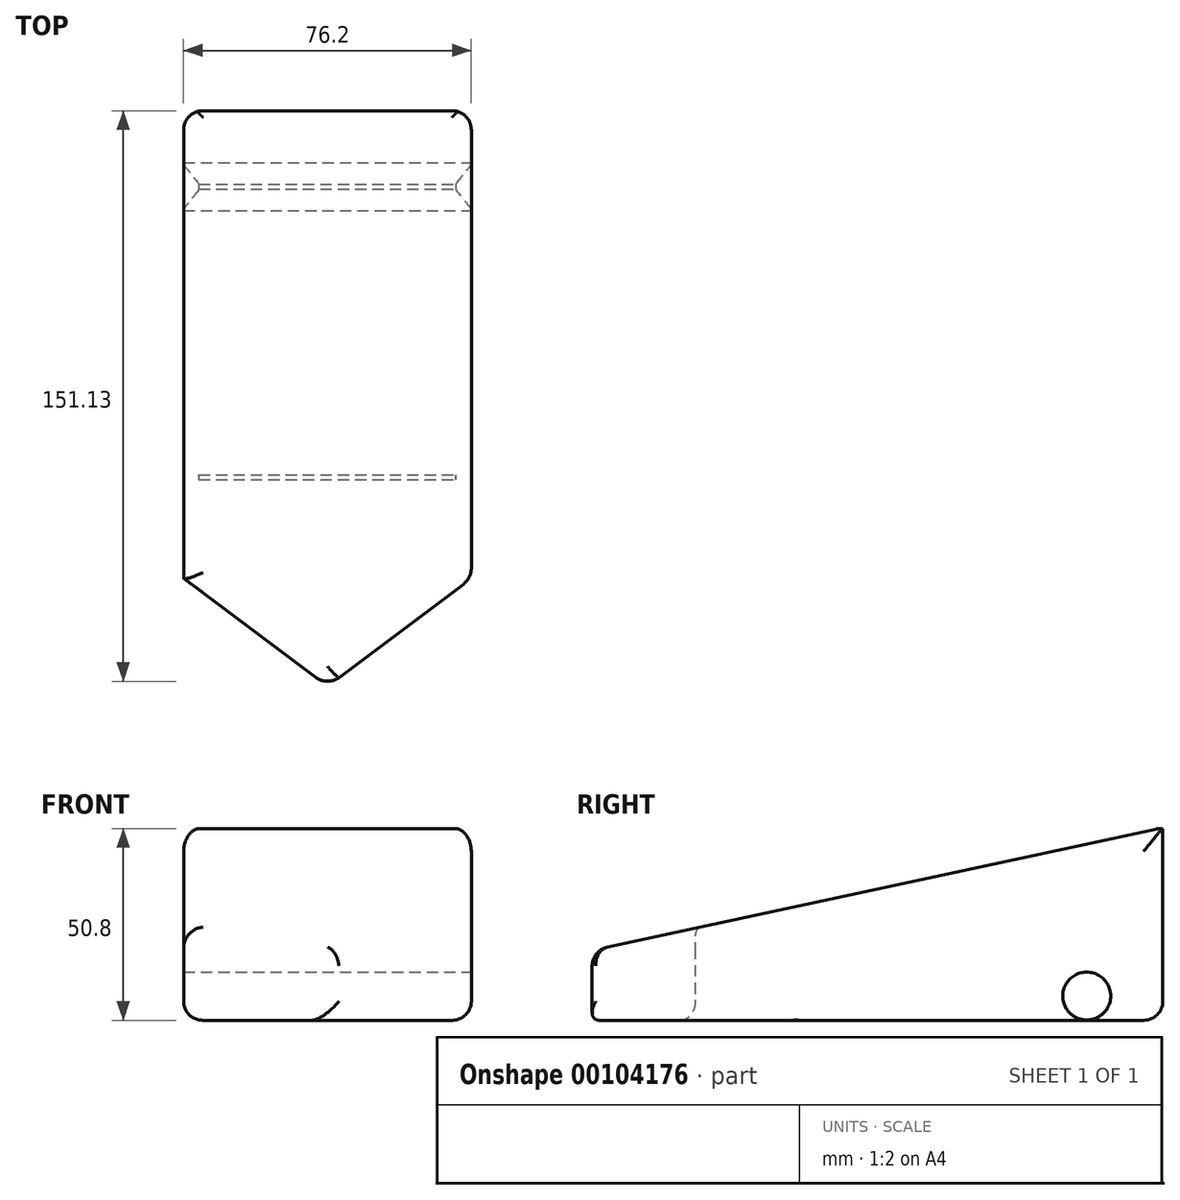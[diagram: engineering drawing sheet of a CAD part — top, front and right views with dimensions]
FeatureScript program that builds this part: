
annotation { "Feature Type Name" : "Feature", "Feature Type Description" : "" }
export const myFeature = defineFeature(function(context is Context, id is Id, definition is map)
    precondition{}
    {
        {
            var Q0;
            Q0=qCreatedBy(makeId("Top.planeOp"),FACE);
            var sketch = newSketch(context, id + "F0", { "sketchPlane" : qUnion([Q0])});
            skLineSegment(sketch, "E0.bottom", {"start": v(-42.93, 33.01) * mm, "end": v(33.27, 33.01) * mm});
            skLineSegment(sketch, "E0.top", {"start": v(-42.93, -119.39) * mm, "end": v(33.27, -119.39) * mm});
            skLineSegment(sketch, "E1", {"start": v(-4.83, -119.39) * mm, "end": v(-42.93, -90.81) * mm});
            skLineSegment(sketch, "E2", {"start": v(-4.83, -119.39) * mm, "end": v(33.27, -90.81) * mm});
            skLineSegment(sketch, "E3", {"start": v(-42.93, -119.39) * mm, "end": v(-42.93, 33.01) * mm});
            skLineSegment(sketch, "E4", {"start": v(33.27, -119.39) * mm, "end": v(33.27, 33.01) * mm});
            skSolve(sketch);
        }
        {
            var Q0;
            Q0 = qSketchRegion(id + "F0", true);
            extrude(context, id + "F1", {"entities" : qUnion([Q0]), "depth" : 50.8 * mm});
        }
        {
            var Q0;
            Q0=makeQuery(id+"F1.opExtrude","SWEPT_FACE",FACE,{"disambiguationData":[OSD([sQuery(id+"F0.wireOp",EDGE,"E4")])]});
            cPlane(context, id + "F2", {"entities" : qUnion([Q0]), "cplaneType" : CPlaneType.OFFSET, "offset" : 0 * mm, "width" : 152.4 * mm, "height" : 152.4 * mm});
        }
        {
            var Q0;
            Q0=qCreatedBy(id+"F2.planeOp",FACE);
            var sketch = newSketch(context, id + "F3", { "sketchPlane" : qUnion([Q0])});
            skLineSegment(sketch, "E5", {"start": v(-119.55, 51.02) * mm, "end": v(-119.55, 0.22) * mm});
            skLineSegment(sketch, "E6", {"start": v(-119.55, 51.02) * mm, "end": v(32.85, 51.02) * mm});
            skCircle(sketch, "E7", {"center": v(-64.12, 6.43) * mm, "radius": 6.35 * mm});
            skLineSegment(sketch, "E8", {"start": v(-64.12, 6.43) * mm, "end": v(12.85, 6.43) * mm});
            skCircle(sketch, "E9", {"center": v(12.85, 6.43) * mm, "radius": 6.35 * mm});
            skLineSegment(sketch, "E10", {"start": v(-64.76, 0.11) * mm, "end": v(13.5, 0.11) * mm});
            skLineSegment(sketch, "E11", {"start": v(-119.55, 18.18) * mm, "end": v(32.85, 51.02) * mm});
            skSolve(sketch);
        }
        {
            var Q0;
            {var subQ0=sQuery(id+"F3.wireOp",EDGE,"E6");Q0=makeQuery(id+"F3.imprint","IMPRINT",FACE,{"disambiguationData":[TD([[makeQuery(id+"F3.imprint","IMPRINT",EDGE,{"derivedFrom":subQ0}),-1.0]])]});}
            extrude(context, id + "F4", {"entities" : qUnion([Q0]), "operationType" : NewBodyOperationType.REMOVE, "oppositeDirection" : true, "depth" : 101.6 * mm});
        }
        {
            var Q0;
            {var subQ3=sQuery(id+"F0.wireOp",EDGE,"E2");Q0=makeQuery(id+"F0.imprint","IMPRINT",FACE,{"disambiguationData":[TD([[makeQuery(id+"F0.imprint","IMPRINT",EDGE,{"derivedFrom":subQ3}),-1.0]])]});}
            var Q1;
            {var subQ3=sQuery(id+"F0.wireOp",EDGE,"E1");Q1=makeQuery(id+"F0.imprint","IMPRINT",FACE,{"disambiguationData":[TD([[makeQuery(id+"F0.imprint","IMPRINT",EDGE,{"derivedFrom":subQ3}),1.0]])]});}
            extrude(context, id + "F5", {"entities" : qUnion([Q0, Q1]), "operationType" : NewBodyOperationType.REMOVE, "depth" : 50.8 * mm});
        }
        {
            var Q0;
            {var subQ0=sQuery(id+"F3.wireOp",EDGE,"E10");var subQ1=sQuery(id+"F3.wireOp",EDGE,"E7");var subQ2=makeQuery(id+"F3.imprint","INTERSECT",VERTEX,{"disambiguationData":[OD(0.0)],"derivedFrom":[subQ1,subQ0]});Q0=makeQuery(id+"F3.imprint","IMPRINT",FACE,{"disambiguationData":[TD([[makeQuery(id+"F3.imprint","IMPRINT",EDGE,{"disambiguationData":[TD([[subQ2,1.0]])],"derivedFrom":subQ1}),1.0]])]});}
            var Q1;
            {var subQ0=sQuery(id+"F3.wireOp",EDGE,"E9");var subQ1=makeQuery(id+"F3.imprint","INTERSECT",VERTEX,{"derivedFrom":[sQuery(id+"F3.wireOp",EDGE,"E8"),subQ0]});Q1=makeQuery(id+"F3.imprint","IMPRINT",FACE,{"disambiguationData":[TD([[makeQuery(id+"F3.imprint","IMPRINT",EDGE,{"disambiguationData":[TD([[subQ1,-1.0]])],"derivedFrom":subQ0}),1.0]])]});}
            extrude(context, id + "F6", {"entities" : qUnion([Q0, Q1]), "operationType" : NewBodyOperationType.REMOVE, "oppositeDirection" : true, "depth" : 76.2 * mm});
        }
        {
            var Q0;
            Q0=makeQuery(id+"F4.boolean.opBoolean","COPY",FACE,{"derivedFrom":makeQuery(id+"F4.opExtrude","SWEPT_FACE",FACE,{"disambiguationData":[OSD([sQuery(id+"F3.wireOp",EDGE,"E11")])]})});
            var Q1;
            Q1=makeQuery(id+"F5.boolean.opBoolean","COPY",FACE,{"derivedFrom":makeQuery(id+"F5.opExtrude","SWEPT_FACE",FACE,{"disambiguationData":[OSD([sQuery(id+"F0.wireOp",EDGE,"E2")])]})});
            var Q2;
            Q2=makeQuery(id+"F5.boolean.opBoolean","INTERSECT",EDGE,{"derivedFrom":[makeQuery(id+"F4.boolean.opBoolean","COPY",FACE,{"derivedFrom":makeQuery(id+"F4.opExtrude","SWEPT_FACE",FACE,{"disambiguationData":[OSD([sQuery(id+"F3.wireOp",EDGE,"E11")])]})}),makeQuery(id+"F5.opExtrude","SWEPT_FACE",FACE,{"disambiguationData":[OSD([sQuery(id+"F0.wireOp",EDGE,"E1")])]})]});
            var Q3;
            Q3=makeQuery(id+"F1.opExtrude","SWEPT_EDGE",EDGE,{"disambiguationData":[OSD([sQuery(id+"F0.wireOp",EDGE,"E0.bottom"),sQuery(id+"F0.wireOp",EDGE,"E4")])]});
            var Q4;
            Q4=makeQuery(id+"F1.opExtrude","SWEPT_EDGE",EDGE,{"disambiguationData":[OSD([sQuery(id+"F0.wireOp",EDGE,"E0.bottom"),sQuery(id+"F0.wireOp",EDGE,"E3")])]});
            var Q5;
            Q5=makeQuery(id+"F1.opExtrude","CAP_EDGE",EDGE,{"disambiguationData":[OSD([sQuery(id+"F0.wireOp",EDGE,"E3")])],"isStart":true});
            var Q6;
            Q6=makeQuery(id+"F1.opExtrude","CAP_EDGE",EDGE,{"disambiguationData":[OSD([sQuery(id+"F0.wireOp",EDGE,"E4")])],"isStart":true});
            var Q7;
            Q7=makeQuery(id+"F1.opExtrude","CAP_EDGE",EDGE,{"disambiguationData":[OSD([sQuery(id+"F0.wireOp",EDGE,"E0.bottom")])],"isStart":true});
            var Q8;
            Q8=makeQuery(id+"F5.boolean.opBoolean","COPY",EDGE,{"derivedFrom":makeQuery(id+"F5.opExtrude","CAP_EDGE",EDGE,{"disambiguationData":[OSD([sQuery(id+"F0.wireOp",EDGE,"E1")])],"isStart":true})});
            fillet(context, id + "F7", {"entities" : qUnion([Q0, Q1, Q2, Q3, Q4, Q5, Q6, Q7, Q8]), "radius" : 5.08 * mm, "tangentPropagation" : true, "allowEdgeOverflow" : false});
        }
    });
